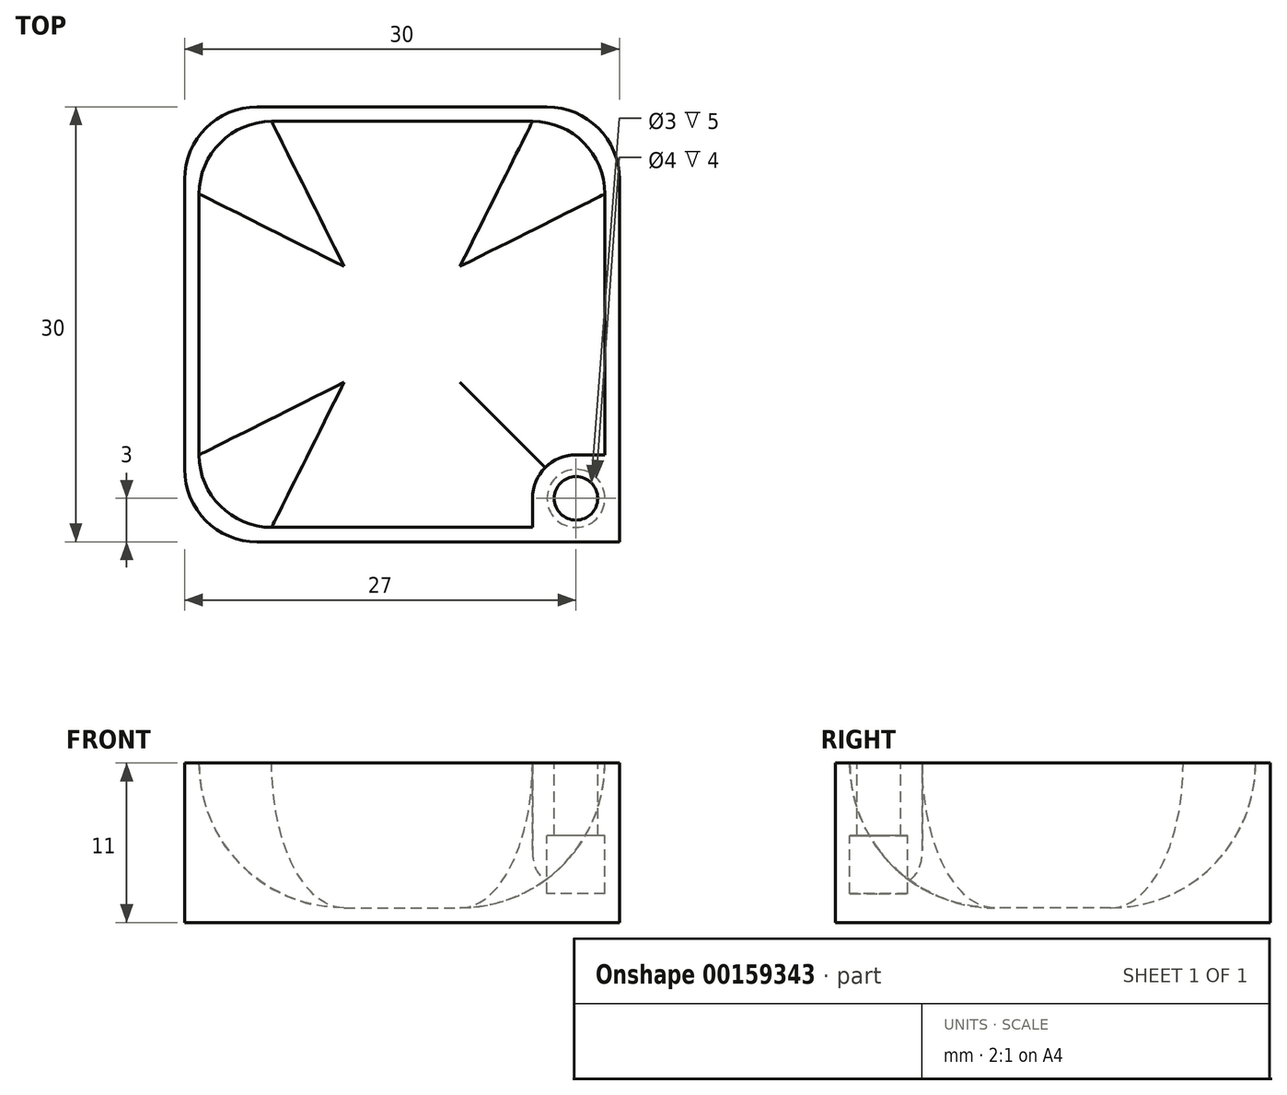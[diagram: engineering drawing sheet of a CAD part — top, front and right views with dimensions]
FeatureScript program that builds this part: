
annotation { "Feature Type Name" : "Feature", "Feature Type Description" : "" }
export const myFeature = defineFeature(function(context is Context, id is Id, definition is map)
    precondition{}
    {
        {
            var Q0;
            Q0=qCreatedBy(makeId("Top.planeOp"),FACE);
            var sketch = newSketch(context, id + "F0", { "sketchPlane" : qUnion([Q0])});
            skLineSegment(sketch, "E0.bottom", {"start": v(-15, 15) * mm, "end": v(15, 15) * mm});
            skLineSegment(sketch, "E0.top", {"start": v(-15, -15) * mm, "end": v(15, -15) * mm});
            skLineSegment(sketch, "E0.left", {"start": v(-15, 15) * mm, "end": v(-15, -15) * mm});
            skLineSegment(sketch, "E0.right", {"start": v(15, 15) * mm, "end": v(15, -15) * mm});
            skPoint(sketch, "E0.middle", {"position": v(0, 0) * mm});
            skSolve(sketch);
        }
        {
            var Q0;
            Q0 = qSketchRegion(id + "F0", true);
            extrude(context, id + "F1", {"entities" : qUnion([Q0]), "depth" : 11 * mm});
        }
        {
            var Q0;
            Q0=makeQuery(id+"F1.opExtrude","CAP_FACE",FACE,{"disambiguationData":[OSD([sQuery(id+"F0.wireOp",EDGE,"E0.bottom"),sQuery(id+"F0.wireOp",EDGE,"E0.top"),sQuery(id+"F0.wireOp",EDGE,"E0.left"),sQuery(id+"F0.wireOp",EDGE,"E0.right")])],"isStart":false});
            var sketch = newSketch(context, id + "F2", { "sketchPlane" : qUnion([Q0])});
            skLineSegment(sketch, "E1.bottom", {"start": v(-14, 14) * mm, "end": v(14, 14) * mm});
            skLineSegment(sketch, "E1.top", {"start": v(-14, -14) * mm, "end": v(14, -14) * mm});
            skLineSegment(sketch, "E1.left", {"start": v(-14, 14) * mm, "end": v(-14, -14) * mm});
            skLineSegment(sketch, "E1.right", {"start": v(14, 14) * mm, "end": v(14, -14) * mm});
            skPoint(sketch, "E1.middle", {"position": v(0, 0) * mm});
            skSolve(sketch);
        }
        {
            var Q0;
            Q0 = qSketchRegion(id + "F2", true);
            extrude(context, id + "F3", {"entities" : qUnion([Q0]), "operationType" : NewBodyOperationType.REMOVE, "oppositeDirection" : true, "depth" : 10 * mm});
        }
        {
            var Q0;
            Q0=makeQuery(id+"F3.boolean.opBoolean","COPY",EDGE,{"derivedFrom":makeQuery(id+"F3.opExtrude","SWEPT_EDGE",EDGE,{"disambiguationData":[OSD([sQuery(id+"F2.wireOp",EDGE,"E1.bottom"),sQuery(id+"F2.wireOp",EDGE,"E1.left")])]})});
            var Q1;
            Q1=makeQuery(id+"F3.boolean.opBoolean","COPY",EDGE,{"derivedFrom":makeQuery(id+"F3.opExtrude","SWEPT_EDGE",EDGE,{"disambiguationData":[OSD([sQuery(id+"F2.wireOp",EDGE,"E1.top"),sQuery(id+"F2.wireOp",EDGE,"E1.left")])]})});
            var Q2;
            Q2=makeQuery(id+"F3.boolean.opBoolean","COPY",EDGE,{"derivedFrom":makeQuery(id+"F3.opExtrude","SWEPT_EDGE",EDGE,{"disambiguationData":[OSD([sQuery(id+"F2.wireOp",EDGE,"E1.bottom"),sQuery(id+"F2.wireOp",EDGE,"E1.right")])]})});
            var Q3;
            Q3=makeQuery(id+"F1.opExtrude","SWEPT_EDGE",EDGE,{"disambiguationData":[OSD([sQuery(id+"F0.wireOp",EDGE,"E0.top"),sQuery(id+"F0.wireOp",EDGE,"E0.left")])]});
            var Q4;
            Q4=makeQuery(id+"F1.opExtrude","SWEPT_EDGE",EDGE,{"disambiguationData":[OSD([sQuery(id+"F0.wireOp",EDGE,"E0.bottom"),sQuery(id+"F0.wireOp",EDGE,"E0.right")])]});
            var Q5;
            Q5=makeQuery(id+"F1.opExtrude","SWEPT_EDGE",EDGE,{"disambiguationData":[OSD([sQuery(id+"F0.wireOp",EDGE,"E0.bottom"),sQuery(id+"F0.wireOp",EDGE,"E0.left")])]});
            fillet(context, id + "F4", {"entities" : qUnion([Q0, Q1, Q2, Q3, Q4, Q5]), "radius" : 5 * mm, "tangentPropagation" : true, "allowEdgeOverflow" : false});
        }
        {
            var Q0;
            Q0=makeQuery(id+"F3.boolean.opBoolean","COPY",EDGE,{"derivedFrom":makeQuery(id+"F3.opExtrude","CAP_EDGE",EDGE,{"disambiguationData":[OSD([sQuery(id+"F2.wireOp",EDGE,"E1.left")])],"isStart":false})});
            fillet(context, id + "F5", {"entities" : qUnion([Q0]), "radius" : 10 * mm, "tangentPropagation" : true, "allowEdgeOverflow" : false});
        }
        {
            var Q0;
            Q0=makeQuery(id+"F1.opExtrude","CAP_FACE",FACE,{"disambiguationData":[OSD([sQuery(id+"F0.wireOp",EDGE,"E0.bottom"),sQuery(id+"F0.wireOp",EDGE,"E0.top"),sQuery(id+"F0.wireOp",EDGE,"E0.left"),sQuery(id+"F0.wireOp",EDGE,"E0.right")])],"isStart":false});
            var sketch = newSketch(context, id + "F6", { "sketchPlane" : qUnion([Q0])});
            skLineSegment(sketch, "E2.bottom", {"start": v(15, -15) * mm, "end": v(9, -15) * mm});
            skLineSegment(sketch, "E2.top", {"start": v(15, -9) * mm, "end": v(9, -9) * mm});
            skLineSegment(sketch, "E2.left", {"start": v(15, -15) * mm, "end": v(15, -9) * mm});
            skLineSegment(sketch, "E2.right", {"start": v(9, -15) * mm, "end": v(9, -9) * mm});
            skSolve(sketch);
        }
        {
            var Q0;
            Q0 = qSketchRegion(id + "F6", true);
            extrude(context, id + "F7", {"entities" : qUnion([Q0]), "operationType" : NewBodyOperationType.ADD, "oppositeDirection" : true, "depth" : 10 * mm});
        }
        {
            var Q0;
            Q0=makeQuery(id+"F7.boolean.opBoolean","MERGE",FACE,{"derivedFrom":[makeQuery(id+"F1.opExtrude","CAP_FACE",FACE,{"disambiguationData":[OSD([sQuery(id+"F0.wireOp",EDGE,"E0.bottom"),sQuery(id+"F0.wireOp",EDGE,"E0.top"),sQuery(id+"F0.wireOp",EDGE,"E0.left"),sQuery(id+"F0.wireOp",EDGE,"E0.right")])],"isStart":false}),makeQuery(id+"F7.opExtrude","CAP_FACE",FACE,{"disambiguationData":[OSD([sQuery(id+"F6.wireOp",EDGE,"E2.bottom"),sQuery(id+"F6.wireOp",EDGE,"E2.top"),sQuery(id+"F6.wireOp",EDGE,"E2.left"),sQuery(id+"F6.wireOp",EDGE,"E2.right")])],"isStart":true})]});
            var sketch = newSketch(context, id + "F8", { "sketchPlane" : qUnion([Q0])});
            skCircle(sketch, "E3", {"center": v(12, -12) * mm, "radius": 1.5 * mm});
            skSolve(sketch);
        }
        {
            var Q0;
            Q0 = qSketchRegion(id + "F8", true);
            extrude(context, id + "F9", {"entities" : qUnion([Q0]), "operationType" : NewBodyOperationType.REMOVE, "oppositeDirection" : true, "depth" : 5 * mm});
        }
        {
            var Q0;
            Q0=makeQuery(id+"F9.boolean.opBoolean","COPY",FACE,{"derivedFrom":makeQuery(id+"F9.opExtrude","CAP_FACE",FACE,{"disambiguationData":[OSD([sQuery(id+"F8.wireOp",EDGE,"E3")])],"isStart":false})});
            var sketch = newSketch(context, id + "F10", { "sketchPlane" : qUnion([Q0])});
            skCircle(sketch, "E4", {"center": v(12, -12) * mm, "radius": 2 * mm});
            skSolve(sketch);
        }
        {
            var Q0;
            Q0 = qSketchRegion(id + "F10", true);
            extrude(context, id + "F11", {"entities" : qUnion([Q0]), "operationType" : NewBodyOperationType.REMOVE, "oppositeDirection" : true, "depth" : 4 * mm});
        }
        {
            var Q0;
            Q0=makeQuery(id+"F7.opExtrude","SWEPT_EDGE",EDGE,{"disambiguationData":[OSD([sQuery(id+"F6.wireOp",EDGE,"E2.top"),sQuery(id+"F6.wireOp",EDGE,"E2.right")])]});
            fillet(context, id + "F12", {"entities" : qUnion([Q0]), "radius" : 3 * mm, "tangentPropagation" : true, "allowEdgeOverflow" : false});
        }
    });
